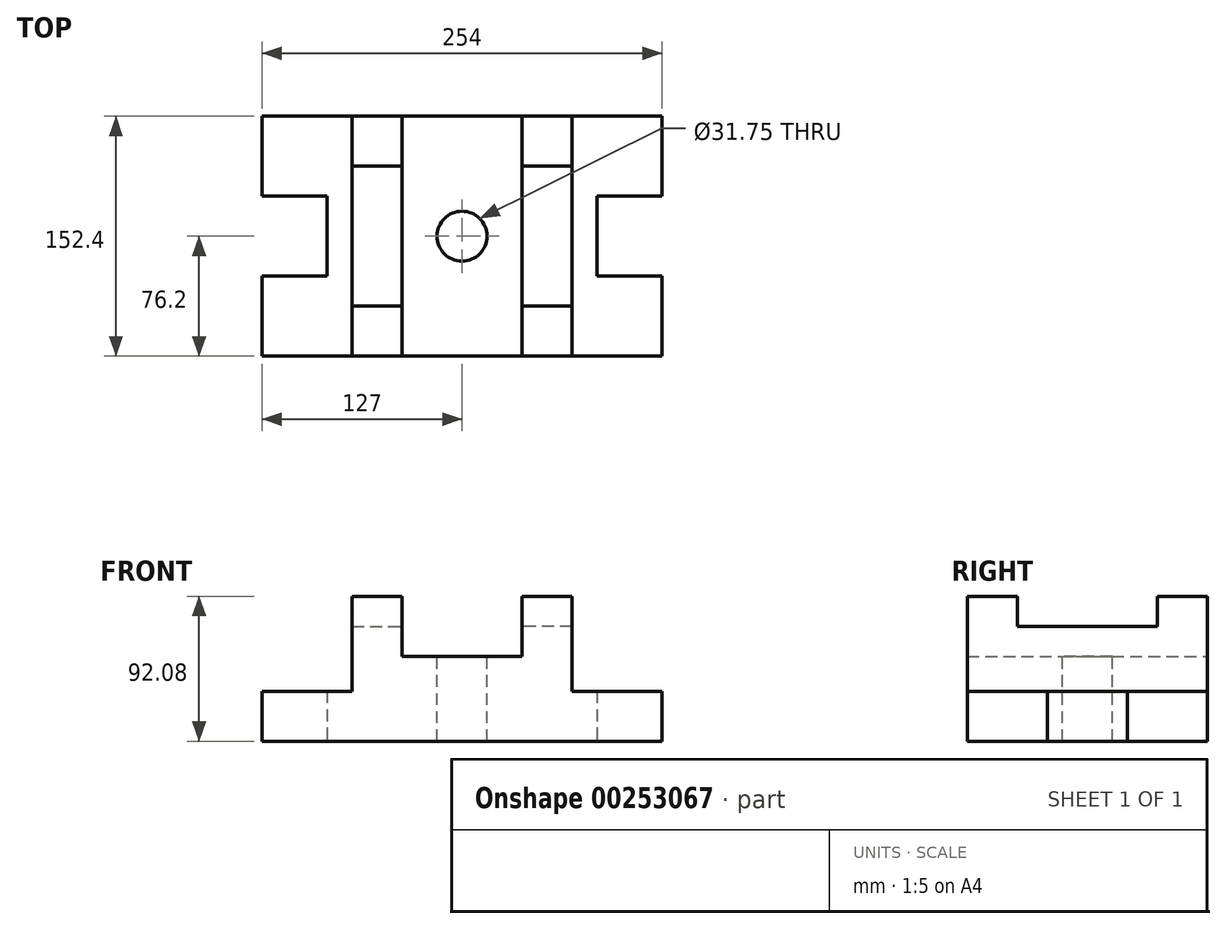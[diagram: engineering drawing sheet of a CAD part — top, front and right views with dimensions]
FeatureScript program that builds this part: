
annotation { "Feature Type Name" : "Feature", "Feature Type Description" : "" }
export const myFeature = defineFeature(function(context is Context, id is Id, definition is map)
    precondition{}
    {
        {
            var Q0;
            Q0=qCreatedBy(makeId("Top.planeOp"),FACE);
            var sketch = newSketch(context, id + "F0", { "sketchPlane" : qUnion([Q0])});
            skLineSegment(sketch, "E0.bottom", {"start": v(127, 76.2) * mm, "end": v(-127, 76.2) * mm});
            skLineSegment(sketch, "E0.top", {"start": v(127, -76.2) * mm, "end": v(-127, -76.2) * mm});
            skLineSegment(sketch, "E0.left", {"start": v(127, 76.2) * mm, "end": v(127, 25.4) * mm});
            skLineSegment(sketch, "E0.right", {"start": v(-127, 76.2) * mm, "end": v(-127, -76.2) * mm});
            skPoint(sketch, "E0.middle", {"position": v(0, 0) * mm});
            skLineSegment(sketch, "E1.bottom", {"start": v(127, 25.4) * mm, "end": v(85.72, 25.4) * mm});
            skLineSegment(sketch, "E1.top", {"start": v(127, -25.4) * mm, "end": v(85.72, -25.4) * mm});
            skLineSegment(sketch, "E1.right", {"start": v(85.72, 25.4) * mm, "end": v(85.72, -25.4) * mm});
            skPoint(sketch, "E1.middle", {"position": v(106.36, 0) * mm});
            skLineSegment(sketch, "E2", {"start": v(0, 0) * mm, "end": v(0, 76.2) * mm, "construction": true});
            skLineSegment(sketch, "E3.MirrorCS", {"start": v(-127, 0) * mm, "end": v(-106.36, 0) * mm, "construction": true});
            skLineSegment(sketch, "E4.MirrorCS", {"start": v(-127, 25.4) * mm, "end": v(-85.72, 25.4) * mm});
            skLineSegment(sketch, "E5.MirrorCS", {"start": v(-127, -25.4) * mm, "end": v(-85.72, -25.4) * mm});
            skLineSegment(sketch, "E6.MirrorCS", {"start": v(-127, 25.4) * mm, "end": v(-127, -25.4) * mm});
            skLineSegment(sketch, "E7.MirrorCS", {"start": v(-85.72, 25.4) * mm, "end": v(-85.73, -25.4) * mm});
            skPoint(sketch, "E8.MirrorP", {"position": v(-106.36, 0) * mm});
            skLineSegment(sketch, "E9.trimOffspring", {"start": v(127, -25.4) * mm, "end": v(127, -76.2) * mm});
            skPoint(sketch, "E10.start.orphan", {"position": v(127, 0) * mm});
            skSolve(sketch);
        }
        {
            var Q0;
            {var subQ0=sQuery(id+"F0.wireOp",EDGE,"E0.bottom");Q0=makeQuery(id+"F0.imprint","IMPRINT",FACE,{"disambiguationData":[TD([[makeQuery(id+"F0.imprint","IMPRINT",EDGE,{"derivedFrom":subQ0}),1.0]])]});}
            extrude(context, id + "F1", {"entities" : qUnion([Q0]), "depth" : 31.75 * mm});
        }
        {
            var Q0;
            Q0=makeQuery(id+"F1.opExtrude","CAP_FACE",FACE,{"disambiguationData":[OSD([sQuery(id+"F0.wireOp",EDGE,"E0.bottom"),sQuery(id+"F0.wireOp",EDGE,"E0.top"),sQuery(id+"F0.wireOp",EDGE,"E0.left"),sQuery(id+"F0.wireOp",EDGE,"E1.bottom"),sQuery(id+"F0.wireOp",EDGE,"E1.top"),sQuery(id+"F0.wireOp",EDGE,"E1.right"),sQuery(id+"F0.wireOp",EDGE,"E0.right"),sQuery(id+"F0.wireOp",EDGE,"E4.MirrorCS"),sQuery(id+"F0.wireOp",EDGE,"E5.MirrorCS"),sQuery(id+"F0.wireOp",EDGE,"E7.MirrorCS")])],"isStart":false});
            var sketch = newSketch(context, id + "F2", { "sketchPlane" : qUnion([Q0])});
            skLineSegment(sketch, "E11.bottom", {"start": v(69.85, 76.2) * mm, "end": v(-69.85, 76.2) * mm});
            skLineSegment(sketch, "E11.top", {"start": v(69.85, -76.2) * mm, "end": v(-69.85, -76.2) * mm});
            skLineSegment(sketch, "E11.left", {"start": v(69.85, 76.2) * mm, "end": v(69.85, -76.2) * mm});
            skLineSegment(sketch, "E11.right", {"start": v(-69.85, 76.2) * mm, "end": v(-69.85, -76.2) * mm});
            skPoint(sketch, "E11.middle", {"position": v(0, 0) * mm});
            skPoint(sketch, "E12.endSnap0", {"position": v(0, 76.2) * mm});
            skSolve(sketch);
        }
        {
            var Q0;
            Q0=makeQuery(id+"F2.imprint","IMPRINT",FACE,{"disambiguationData":[TD([[makeQuery(id+"F2.imprint","IMPRINT",EDGE,{"derivedFrom":sQuery(id+"F2.wireOp",EDGE,"E11.bottom")}),1.0]])]});
            extrude(context, id + "F3", {"entities" : qUnion([Q0]), "operationType" : NewBodyOperationType.ADD, "depth" : 22.22 * mm});
        }
        {
            var Q0;
            Q0=makeQuery(id+"F3.opExtrude","CAP_FACE",FACE,{"disambiguationData":[OSD([sQuery(id+"F2.wireOp",EDGE,"E11.bottom"),sQuery(id+"F2.wireOp",EDGE,"E11.top"),sQuery(id+"F2.wireOp",EDGE,"E11.left"),sQuery(id+"F2.wireOp",EDGE,"E11.right")])],"isStart":false});
            var sketch = newSketch(context, id + "F4", { "sketchPlane" : qUnion([Q0])});
            skLineSegment(sketch, "E13.bottom", {"start": v(-69.85, -76.2) * mm, "end": v(-38.1, -76.2) * mm});
            skLineSegment(sketch, "E13.top", {"start": v(-69.85, 76.2) * mm, "end": v(-38.1, 76.2) * mm});
            skLineSegment(sketch, "E13.left", {"start": v(-69.85, -76.2) * mm, "end": v(-69.85, 76.2) * mm});
            skLineSegment(sketch, "E13.right", {"start": v(-38.1, -76.2) * mm, "end": v(-38.1, 76.2) * mm});
            skLineSegment(sketch, "E14.bottom", {"start": v(69.85, -76.2) * mm, "end": v(38.1, -76.2) * mm});
            skLineSegment(sketch, "E14.top", {"start": v(69.85, 76.2) * mm, "end": v(38.1, 76.2) * mm});
            skLineSegment(sketch, "E14.left", {"start": v(69.85, -76.2) * mm, "end": v(69.85, 76.2) * mm});
            skLineSegment(sketch, "E14.right", {"start": v(38.1, -76.2) * mm, "end": v(38.1, 76.2) * mm});
            skCircle(sketch, "E15", {"center": v(0, 0) * mm, "radius": 15.88 * mm});
            skLineSegment(sketch, "E16", {"start": v(0, 0) * mm, "end": v(0, -76.2) * mm, "construction": true});
            skSolve(sketch);
        }
        {
            var Q0;
            Q0=makeQuery(id+"F4.imprint","IMPRINT",FACE,{"disambiguationData":[TD([[makeQuery(id+"F4.imprint","IMPRINT",EDGE,{"derivedFrom":sQuery(id+"F4.wireOp",EDGE,"E14.bottom")}),-1.0]])]});
            var Q1;
            Q1=makeQuery(id+"F4.imprint","IMPRINT",FACE,{"disambiguationData":[TD([[makeQuery(id+"F4.imprint","IMPRINT",EDGE,{"derivedFrom":sQuery(id+"F4.wireOp",EDGE,"E13.bottom")}),-1.0]])]});
            extrude(context, id + "F5", {"entities" : qUnion([Q0, Q1]), "operationType" : NewBodyOperationType.ADD, "depth" : 19.05 * mm});
        }
        {
            var Q0;
            Q0=makeQuery(id+"F5.opExtrude","CAP_FACE",FACE,{"disambiguationData":[OSD([sQuery(id+"F4.wireOp",EDGE,"E13.bottom"),sQuery(id+"F4.wireOp",EDGE,"E13.top"),sQuery(id+"F4.wireOp",EDGE,"E13.left"),sQuery(id+"F4.wireOp",EDGE,"E13.right")])],"isStart":false});
            var sketch = newSketch(context, id + "F6", { "sketchPlane" : qUnion([Q0])});
            skLineSegment(sketch, "E17.bottom", {"start": v(-69.85, 76.2) * mm, "end": v(-38.1, 76.2) * mm});
            skLineSegment(sketch, "E17.top", {"start": v(-69.85, 44.45) * mm, "end": v(-38.1, 44.45) * mm});
            skLineSegment(sketch, "E17.left", {"start": v(-69.85, 76.2) * mm, "end": v(-69.85, 44.45) * mm});
            skLineSegment(sketch, "E17.right", {"start": v(-38.1, 76.2) * mm, "end": v(-38.1, 44.45) * mm});
            skLineSegment(sketch, "E18.bottom", {"start": v(-69.85, -76.2) * mm, "end": v(-38.1, -76.2) * mm});
            skLineSegment(sketch, "E18.top", {"start": v(-69.85, -44.45) * mm, "end": v(-38.1, -44.45) * mm});
            skLineSegment(sketch, "E18.left", {"start": v(-69.85, -76.2) * mm, "end": v(-69.85, -44.45) * mm});
            skLineSegment(sketch, "E18.right", {"start": v(-38.1, -76.2) * mm, "end": v(-38.1, -44.45) * mm});
            skSolve(sketch);
        }
        {
            var Q0;
            Q0=makeQuery(id+"F5.opExtrude","CAP_FACE",FACE,{"disambiguationData":[OSD([sQuery(id+"F4.wireOp",EDGE,"E14.bottom"),sQuery(id+"F4.wireOp",EDGE,"E14.top"),sQuery(id+"F4.wireOp",EDGE,"E14.left"),sQuery(id+"F4.wireOp",EDGE,"E14.right")])],"isStart":false});
            var sketch = newSketch(context, id + "F7", { "sketchPlane" : qUnion([Q0])});
            skLineSegment(sketch, "E19.bottom", {"start": v(69.85, 76.2) * mm, "end": v(38.1, 76.2) * mm});
            skLineSegment(sketch, "E19.top", {"start": v(69.85, 44.45) * mm, "end": v(38.1, 44.45) * mm});
            skLineSegment(sketch, "E19.left", {"start": v(69.85, 76.2) * mm, "end": v(69.85, 44.45) * mm});
            skLineSegment(sketch, "E19.right", {"start": v(38.1, 76.2) * mm, "end": v(38.1, 44.45) * mm});
            skLineSegment(sketch, "E20.bottom", {"start": v(69.85, -76.2) * mm, "end": v(38.1, -76.2) * mm});
            skLineSegment(sketch, "E20.top", {"start": v(69.85, -44.45) * mm, "end": v(38.1, -44.45) * mm});
            skLineSegment(sketch, "E20.left", {"start": v(69.85, -76.2) * mm, "end": v(69.85, -44.45) * mm});
            skLineSegment(sketch, "E20.right", {"start": v(38.1, -76.2) * mm, "end": v(38.1, -44.45) * mm});
            skSolve(sketch);
        }
        {
            var Q0;
            Q0=makeQuery(id+"F6.imprint","IMPRINT",FACE,{"disambiguationData":[TD([[makeQuery(id+"F6.imprint","IMPRINT",EDGE,{"derivedFrom":sQuery(id+"F6.wireOp",EDGE,"E17.bottom")}),1.0]])]});
            var Q1;
            Q1=makeQuery(id+"F6.imprint","IMPRINT",FACE,{"disambiguationData":[TD([[makeQuery(id+"F6.imprint","IMPRINT",EDGE,{"derivedFrom":sQuery(id+"F6.wireOp",EDGE,"E18.bottom")}),-1.0]])]});
            var Q2;
            Q2=makeQuery(id+"F7.imprint","IMPRINT",FACE,{"disambiguationData":[TD([[makeQuery(id+"F7.imprint","IMPRINT",EDGE,{"derivedFrom":sQuery(id+"F7.wireOp",EDGE,"E20.bottom")}),-1.0]])]});
            var Q3;
            Q3=makeQuery(id+"F7.imprint","IMPRINT",FACE,{"disambiguationData":[TD([[makeQuery(id+"F7.imprint","IMPRINT",EDGE,{"derivedFrom":sQuery(id+"F7.wireOp",EDGE,"E19.bottom")}),1.0]])]});
            extrude(context, id + "F8", {"entities" : qUnion([Q0, Q1, Q2, Q3]), "operationType" : NewBodyOperationType.ADD, "depth" : 19.05 * mm});
        }
        {
            var Q0;
            Q0=makeQuery(id+"F3.opExtrude","CAP_FACE",FACE,{"disambiguationData":[OSD([sQuery(id+"F2.wireOp",EDGE,"E11.bottom"),sQuery(id+"F2.wireOp",EDGE,"E11.top"),sQuery(id+"F2.wireOp",EDGE,"E11.left"),sQuery(id+"F2.wireOp",EDGE,"E11.right")])],"isStart":false});
            var sketch = newSketch(context, id + "F9", { "sketchPlane" : qUnion([Q0])});
            skLineSegment(sketch, "E21", {"start": v(0, -76.2) * mm, "end": v(0, 0) * mm, "construction": true});
            skCircle(sketch, "E22", {"center": v(0, 0) * mm, "radius": 15.88 * mm});
            skSolve(sketch);
        }
        {
            var Q0;
            Q0=qSketchRegion(id+"F9",true);
            extrude(context, id + "F10", {"entities" : qUnion([Q0]), "operationType" : NewBodyOperationType.REMOVE, "endBound" : BoundingType.THROUGH_ALL, "oppositeDirection" : true, "depth" : 274.32 * mm});
        }
    });
